# Revit family: 28701x_3_70
name_source: partatom
category: Generic Models
units: mm (PartAtom-declared; Revit-internal decimal feet)

## family parameters
Always vertical = Yes
Can host rebar = No
Cut with Voids When Loaded = No
Part Type = Normal
Room Calculation Point = No
Round Connector Dimension = Use Diameter
Shared = Yes
Work Plane-Based = No

## types (1)
- 28701X
    4.010.00.2 Sheet number of the guideline = 4
    4.010.00.4 Manufacturer name = KESSEL AG
    4.010.00.8 Producer ID number = 4026092000007
    4.100.00.4 Product indentification = Entwässerung
    4.100.00.6 Product classification = Hebeanlagen
    4.110.00.4 Product indentification = Hebeanlage Aqualift F Compact
    4.110.00.5 Main groups of wares = Aqualift F Compact
    4.110.00.6 Product classification = Hebeanlage
    4.500.00.3 Variant / Variant type / Accessories-name = Kunststoff, Edelstahl
    4.700.00.10 Phase = 1/N/PE 230V
    4.700.00.11 Stern-/Dreieck-Anlaufschaltung bei Dreiphasenanschluss oder Drehstrom = nein
    4.700.00.12 Frequency = 50
    4.700.00.13 Type of protection = IP 68
    4.700.00.14 Heat class = F
    4.700.00.16 Maximum temperature of pumped medium = 40 °C
    4.700.00.17 Minimum temperature of pumped medium = 0 °C
    4.700.00.23 Nominal speed of motor = 7.427098
    4.700.00.24 Nominal speed / maximum speed n = 46.666667
    4.700.00.26 Maximum power consumption per pump / drive = 0
    4.700.00.27 Starting current = 5
    4.700.00.4 Product indentification = Hebeanlage Aqualift F Compact, Mono, SPZ 1000, Bodenpl., befliesbar
    4.700.00.7 Nominal connection size on pressure side = DN32, DA40
    4.700.00.8 Nominal connection size on suction side = DN32, DA40
    4.700.00.9 Voltage = 2475.699396
    4.710.01.3 Identifier for closed-loop control = 40
    4.710.01.4 Designation of closed-loop control = 20
    4.710.01.5 Load regulation = 1
    4.710.03.3 Type of dimensions = 2
    4.710.03.4 Length = 670 mm  [stored 2.19816 ft]
    4.710.03.5 Width = 590 mm  [stored 1.9357 ft]
    4.810.00.3 Producer order number = 28701X
    4.810.00.4 DATANORM number = 28701X
    4.810.00.6 GTIN number = 4026092093382
    4.810.00.7 Media- connection number = 9
    ARTICLENO = NB
    BOMINFO = LINA
    CATALOG = KESSEL
    Default Elevation = 0 mm  [stored 0 ft]
    L = 70
    LINA = 28701X
    LINK = https://www.kessel.de
    LMAX = 180
    LMIN = 70
    Manufacturer = KESSEL
    Model = 28701X
    NB = 28701X_3_70
    NBSYN = $SA810ID03._$IDNR._$L.
    NN = Lifting station Aqualift F Compact
    PRC_SPECIFICATIONLINK = https://ausschreiben.de
    PROCUREDATALASTUPDATE = 2024-05-22T12:18:00.399843674+01:00
    PROCURELINK = p.caden.as/kessel/28701X
    PROCUREWEBLINK = https://p.caden.as
    SA200ID03 = 6
    SA250ID03 = vertical
    SA260ID03 = dry-rotor pump
    SA300ID03 = single-level
    SA350ID03 = normal-priming
    SA400ID03 = e-motor for alternating current
    SA460ID03 = direct
    SA700ID07 = 100
    SA700ID21 = 1000
    SA700ID28 = durchgehend
    SA700ID29 = RWDR
    SA700ID30 = 1
    SA700ID31 = 1
    SA700ID32 = 36.60 kg
    SA700ID33 = 1 W
    SA700ID34 = 11.5
    SA700ID37 = 10000 mm
    SA700ID46 = Yes
    SA700ID48 = No
    SUPPLIER = KESSEL

note: [stored X ft] marks values corroborated as IEEE doubles in the binary element streams (Revit-internal decimal feet)

## geometry (parser evidence)
native form markers: Sweep x19
no freeform markers — native parametric forms only
